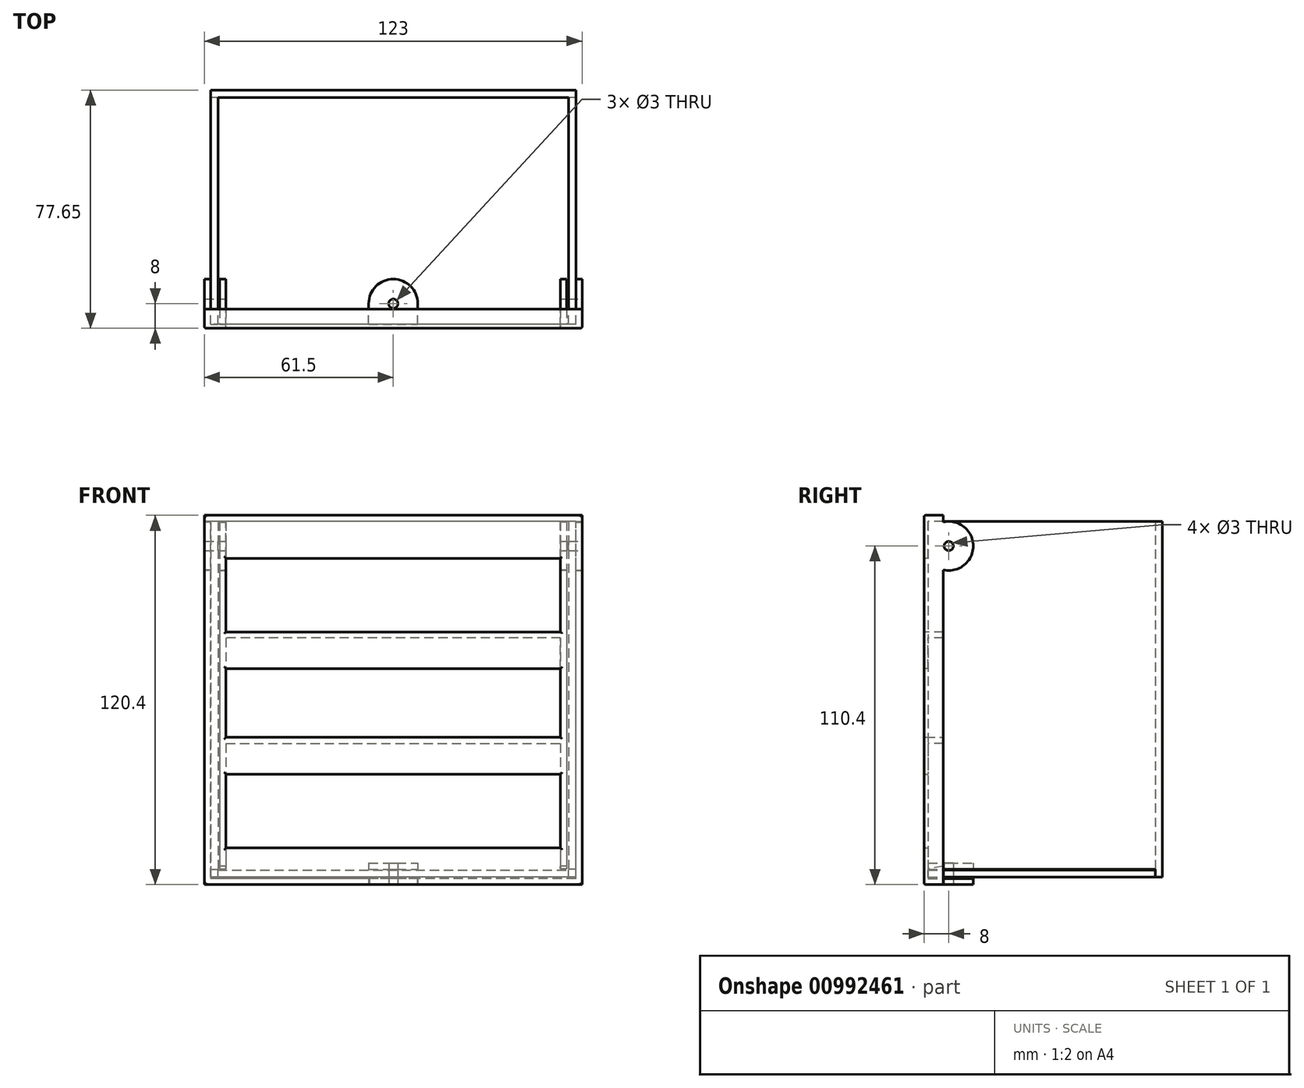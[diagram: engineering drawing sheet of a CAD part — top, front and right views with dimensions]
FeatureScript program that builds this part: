
annotation { "Feature Type Name" : "Feature", "Feature Type Description" : "" }
export const myFeature = defineFeature(function(context is Context, id is Id, definition is map)
    precondition{}
    {
        {
            var Q0;
            Q0=qCreatedBy(makeId("Front.planeOp"),FACE);
            var sketch = newSketch(context, id + "F0", { "sketchPlane" : qUnion([Q0])});
            skLineSegment(sketch, "E0.bottom", {"start": v(59.5, 0) * mm, "end": v(-59.5, 0) * mm});
            skLineSegment(sketch, "E0.top", {"start": v(59.5, 116) * mm, "end": v(-59.5, 116) * mm});
            skLineSegment(sketch, "E0.left", {"start": v(59.5, 0) * mm, "end": v(59.5, 116) * mm});
            skLineSegment(sketch, "E0.right", {"start": v(-59.5, 0) * mm, "end": v(-59.5, 116) * mm});
            skPoint(sketch, "E0.middle", {"position": v(0, 58) * mm});
            skSolve(sketch);
        }
        {
            var Q0;
            Q0=qSketchRegion(id+"F0",true);
            extrude(context, id + "F1", {"entities" : qUnion([Q0]), "oppositeDirection" : true, "depth" : 2.4 * mm, "offsetDistance" : 25 * mm});
        }
        {
            var Q0;
            Q0=makeQuery(id+"F1.opExtrude","CAP_FACE",FACE,{"disambiguationData":[OSD([sQuery(id+"F0.wireOp",EDGE,"E0.bottom"),sQuery(id+"F0.wireOp",EDGE,"E0.top"),sQuery(id+"F0.wireOp",EDGE,"E0.left"),sQuery(id+"F0.wireOp",EDGE,"E0.right")])],"isStart":true});
            var sketch = newSketch(context, id + "F2", { "sketchPlane" : qUnion([Q0])});
            skLineSegment(sketch, "E1.bottom", {"start": v(-59.5, 116) * mm, "end": v(-57.1, 116) * mm});
            skLineSegment(sketch, "E1.top", {"start": v(-59.5, 2.6) * mm, "end": v(-57.1, 2.6) * mm});
            skLineSegment(sketch, "E1.left", {"start": v(-59.5, 116) * mm, "end": v(-59.5, 2.6) * mm});
            skLineSegment(sketch, "E1.right", {"start": v(-57.1, 116) * mm, "end": v(-57.1, 2.6) * mm});
            skLineSegment(sketch, "E2.bottom", {"start": v(59.5, 116) * mm, "end": v(57.1, 116) * mm});
            skLineSegment(sketch, "E2.top", {"start": v(59.5, 2.6) * mm, "end": v(57.1, 2.6) * mm});
            skLineSegment(sketch, "E2.left", {"start": v(59.5, 116) * mm, "end": v(59.5, 2.6) * mm});
            skLineSegment(sketch, "E2.right", {"start": v(57.1, 116) * mm, "end": v(57.1, 2.6) * mm});
            skSolve(sketch);
        }
        {
            var Q0;
            Q0=qSketchRegion(id+"F2",true);
            extrude(context, id + "F3", {"entities" : qUnion([Q0]), "operationType" : NewBodyOperationType.ADD, "depth" : 74 * mm, "offsetDistance" : 25 * mm});
        }
        {
            var Q0;
            Q0=makeQuery(id+"F1.opExtrude","CAP_FACE",FACE,{"disambiguationData":[OSD([sQuery(id+"F0.wireOp",EDGE,"E0.bottom"),sQuery(id+"F0.wireOp",EDGE,"E0.top"),sQuery(id+"F0.wireOp",EDGE,"E0.left"),sQuery(id+"F0.wireOp",EDGE,"E0.right")])],"isStart":true});
            var sketch = newSketch(context, id + "F4", { "sketchPlane" : qUnion([Q0])});
            skLineSegment(sketch, "E3.bottom", {"start": v(-57.1, 0) * mm, "end": v(57.1, 0) * mm});
            skLineSegment(sketch, "E3.top", {"start": v(-57.1, 2.4) * mm, "end": v(57.1, 2.4) * mm});
            skLineSegment(sketch, "E3.left", {"start": v(-57.1, 0) * mm, "end": v(-57.1, 2.4) * mm});
            skLineSegment(sketch, "E3.right", {"start": v(57.1, 0) * mm, "end": v(57.1, 2.4) * mm});
            skSolve(sketch);
        }
        {
            var Q0;
            Q0=qSketchRegion(id+"F4",true);
            var Q1;
            Q1=makeQuery(id+"F3.opExtrude","CAP_FACE",FACE,{"disambiguationData":[OSD([sQuery(id+"F2.wireOp",EDGE,"E1.bottom"),sQuery(id+"F2.wireOp",EDGE,"E1.top"),sQuery(id+"F2.wireOp",EDGE,"E1.left"),sQuery(id+"F2.wireOp",EDGE,"E1.right")])],"isStart":false});
            extrude(context, id + "F5", {"entities" : qUnion([Q0]), "operationType" : NewBodyOperationType.ADD, "endBound" : BoundingType.UP_TO_SURFACE, "depth" : 36.25 * mm, "endBoundEntityFace" : qUnion([Q1]), "offsetDistance" : 25 * mm});
        }
        {
            var Q0;
            Q0=makeQuery(id+"F3.opExtrude","CAP_FACE",FACE,{"disambiguationData":[OSD([sQuery(id+"F2.wireOp",EDGE,"E1.bottom"),sQuery(id+"F2.wireOp",EDGE,"E1.top"),sQuery(id+"F2.wireOp",EDGE,"E1.left"),sQuery(id+"F2.wireOp",EDGE,"E1.right")])],"isStart":false});
            var sketch = newSketch(context, id + "F6", { "sketchPlane" : qUnion([Q0])});
            skLineSegment(sketch, "E4.bottom", {"start": v(59.5, 116) * mm, "end": v(-59.5, 116) * mm});
            skLineSegment(sketch, "E4.top", {"start": v(59.5, 104) * mm, "end": v(-59.5, 104) * mm});
            skLineSegment(sketch, "E4.left", {"start": v(59.5, 116) * mm, "end": v(59.5, 104) * mm});
            skPoint(sketch, "E4.middle", {"position": v(0, 110) * mm});
            skLineSegment(sketch, "E5.bottom", {"start": v(59.5, 80) * mm, "end": v(-59.5, 80) * mm});
            skLineSegment(sketch, "E5.top", {"start": v(59.5, 68) * mm, "end": v(-59.5, 68) * mm});
            skLineSegment(sketch, "E5.left", {"start": v(59.5, 80) * mm, "end": v(59.5, 68) * mm});
            skLineSegment(sketch, "E5.right", {"start": v(-59.5, 80) * mm, "end": v(-59.5, 68) * mm});
            skPoint(sketch, "E5.middle", {"position": v(0, 74) * mm});
            skLineSegment(sketch, "E6.bottom", {"start": v(59.5, 9.6) * mm, "end": v(-59.5, 9.6) * mm});
            skLineSegment(sketch, "E6.top", {"start": v(59.5, -2.4) * mm, "end": v(-59.5, -2.4) * mm});
            skLineSegment(sketch, "E6.left", {"start": v(59.5, 9.6) * mm, "end": v(59.5, -2.4) * mm});
            skLineSegment(sketch, "E6.right", {"start": v(-59.5, 9.6) * mm, "end": v(-59.5, -2.4) * mm});
            skPoint(sketch, "E6.middle", {"position": v(0, 3.6) * mm});
            skLineSegment(sketch, "E7.bottom", {"start": v(59.5, 45.6) * mm, "end": v(-59.5, 45.6) * mm});
            skLineSegment(sketch, "E7.top", {"start": v(59.5, 33.6) * mm, "end": v(-59.5, 33.6) * mm});
            skLineSegment(sketch, "E7.left", {"start": v(59.5, 45.6) * mm, "end": v(59.5, 33.6) * mm});
            skLineSegment(sketch, "E7.right", {"start": v(-59.5, 45.6) * mm, "end": v(-59.5, 33.6) * mm});
            skPoint(sketch, "E7.middle", {"position": v(0, 39.6) * mm});
            skLineSegment(sketch, "E8", {"start": v(-59.5, 116) * mm, "end": v(-59.5, 104) * mm});
            skSolve(sketch);
        }
        {
            var Q0;
            Q0=qSketchRegion(id+"F6",true);
            extrude(context, id + "F7", {"entities" : qUnion([Q0]), "depth" : 1.25 * mm, "offsetDistance" : 25 * mm});
        }
        {
            var Q0;
            Q0=makeQuery(id+"F3.opExtrude","CAP_FACE",FACE,{"disambiguationData":[OSD([sQuery(id+"F2.wireOp",EDGE,"E2.bottom"),sQuery(id+"F2.wireOp",EDGE,"E2.top"),sQuery(id+"F2.wireOp",EDGE,"E2.left"),sQuery(id+"F2.wireOp",EDGE,"E2.right")])],"isStart":false});
            var sketch = newSketch(context, id + "F8", { "sketchPlane" : qUnion([Q0])});
            skLineSegment(sketch, "E9.bottom", {"start": v(61.5, 116) * mm, "end": v(59.5, 116) * mm});
            skLineSegment(sketch, "E9.top", {"start": v(61.5, -2.4) * mm, "end": v(59.5, -2.4) * mm});
            skLineSegment(sketch, "E9.left", {"start": v(61.5, 116) * mm, "end": v(61.5, -2.4) * mm});
            skLineSegment(sketch, "E9.right", {"start": v(59.5, 116) * mm, "end": v(59.5, -2.4) * mm});
            skLineSegment(sketch, "E10.bottom", {"start": v(-59.5, 116) * mm, "end": v(-61.5, 116) * mm});
            skLineSegment(sketch, "E10.top", {"start": v(-59.5, -2.4) * mm, "end": v(-61.5, -2.4) * mm});
            skLineSegment(sketch, "E10.left", {"start": v(-59.5, 116) * mm, "end": v(-59.5, -2.4) * mm});
            skLineSegment(sketch, "E10.right", {"start": v(-61.5, 116) * mm, "end": v(-61.5, -2.4) * mm});
            skLineSegment(sketch, "E11.bottom", {"start": v(56.5, 116) * mm, "end": v(54.5, 116) * mm});
            skLineSegment(sketch, "E11.top", {"start": v(56.5, 2.6) * mm, "end": v(54.5, 2.6) * mm});
            skLineSegment(sketch, "E11.left", {"start": v(56.5, 116) * mm, "end": v(56.5, 2.6) * mm});
            skLineSegment(sketch, "E11.right", {"start": v(54.5, 116) * mm, "end": v(54.5, 2.6) * mm});
            skLineSegment(sketch, "E12.bottom", {"start": v(-56.5, 116) * mm, "end": v(-54.5, 116) * mm});
            skLineSegment(sketch, "E12.top", {"start": v(-56.5, 2.6) * mm, "end": v(-54.5, 2.6) * mm});
            skLineSegment(sketch, "E12.left", {"start": v(-56.5, 116) * mm, "end": v(-56.5, 2.6) * mm});
            skLineSegment(sketch, "E12.right", {"start": v(-54.5, 116) * mm, "end": v(-54.5, 2.6) * mm});
            skSolve(sketch);
        }
        {
            var Q0;
            Q0=qSketchRegion(id+"F8",true);
            var Q1;
            Q1=makeQuery(id+"F7.opExtrude","CAP_FACE",FACE,{"disambiguationData":[OSD([sQuery(id+"F6.wireOp",EDGE,"E6.bottom"),sQuery(id+"F6.wireOp",EDGE,"E6.top"),sQuery(id+"F6.wireOp",EDGE,"E6.left"),sQuery(id+"F6.wireOp",EDGE,"E6.right")])],"isStart":false});
            extrude(context, id + "F9", {"entities" : qUnion([Q0]), "oppositeDirection" : true, "depth" : 5 * mm, "offsetDistance" : 25 * mm, "hasSecondDirection" : true, "secondDirectionBound" : SecondDirectionBoundingType.UP_TO_SURFACE, "secondDirectionOppositeDirection" : false, "secondDirectionDepth" : 2.4 * mm, "secondDirectionBoundEntityFace" : qUnion([Q1])});
        }
        {
            var Q0;
            Q0=makeQuery(id+"F7.opExtrude","SWEPT_BODY",BODY,{"disambiguationData":[OSD([sQuery(id+"F6.wireOp",EDGE,"E6.bottom"),sQuery(id+"F6.wireOp",EDGE,"E6.top"),sQuery(id+"F6.wireOp",EDGE,"E6.left"),sQuery(id+"F6.wireOp",EDGE,"E6.right")])]});
            var Q1;
            Q1=makeQuery(id+"F7.opExtrude","SWEPT_BODY",BODY,{"disambiguationData":[OSD([sQuery(id+"F6.wireOp",EDGE,"E7.bottom"),sQuery(id+"F6.wireOp",EDGE,"E7.top"),sQuery(id+"F6.wireOp",EDGE,"E7.left"),sQuery(id+"F6.wireOp",EDGE,"E7.right")])]});
            var Q2;
            Q2=makeQuery(id+"F9.opExtrude","SWEPT_BODY",BODY,{"disambiguationData":[OSD([sQuery(id+"F8.wireOp",EDGE,"E11.bottom"),sQuery(id+"F8.wireOp",EDGE,"E11.top"),sQuery(id+"F8.wireOp",EDGE,"E11.left"),sQuery(id+"F8.wireOp",EDGE,"E11.right")])]});
            var Q3;
            Q3=makeQuery(id+"F7.opExtrude","SWEPT_BODY",BODY,{"disambiguationData":[OSD([sQuery(id+"F6.wireOp",EDGE,"E4.bottom"),sQuery(id+"F6.wireOp",EDGE,"E4.top"),sQuery(id+"F6.wireOp",EDGE,"E4.left"),sQuery(id+"F6.wireOp",EDGE,"E8")])]});
            var Q4;
            Q4=makeQuery(id+"F9.opExtrude","SWEPT_BODY",BODY,{"disambiguationData":[OSD([sQuery(id+"F8.wireOp",EDGE,"E9.bottom"),sQuery(id+"F8.wireOp",EDGE,"E9.top"),sQuery(id+"F8.wireOp",EDGE,"E9.left"),sQuery(id+"F8.wireOp",EDGE,"E9.right")])]});
            var Q5;
            Q5=makeQuery(id+"F7.opExtrude","SWEPT_BODY",BODY,{"disambiguationData":[OSD([sQuery(id+"F6.wireOp",EDGE,"E5.bottom"),sQuery(id+"F6.wireOp",EDGE,"E5.top"),sQuery(id+"F6.wireOp",EDGE,"E5.left"),sQuery(id+"F6.wireOp",EDGE,"E5.right")])]});
            var Q6;
            Q6=makeQuery(id+"F9.opExtrude","SWEPT_BODY",BODY,{"disambiguationData":[OSD([sQuery(id+"F8.wireOp",EDGE,"E10.bottom"),sQuery(id+"F8.wireOp",EDGE,"E10.top"),sQuery(id+"F8.wireOp",EDGE,"E10.left"),sQuery(id+"F8.wireOp",EDGE,"E10.right")])]});
            var Q7;
            Q7=makeQuery(id+"F9.opExtrude","SWEPT_BODY",BODY,{"disambiguationData":[OSD([sQuery(id+"F8.wireOp",EDGE,"E12.bottom"),sQuery(id+"F8.wireOp",EDGE,"E12.top"),sQuery(id+"F8.wireOp",EDGE,"E12.left"),sQuery(id+"F8.wireOp",EDGE,"E12.right")])]});
            booleanBodies(context, id + "F10", {"operationType" : BooleanOperationType.UNION, "tools" : qUnion([Q0, Q1, Q2, Q3, Q4, Q5, Q6, Q7])});
        }
        {
            var Q0;
            Q0=makeQuery(id+"F9.opExtrude","SWEPT_FACE",FACE,{"disambiguationData":[OSD([sQuery(id+"F8.wireOp",EDGE,"E12.top")])]});
            var sketch = newSketch(context, id + "F11", { "sketchPlane" : qUnion([Q0])});
            skArc(sketch, "E13", {"start": v(-8, 67.25) * mm, "mid": v(0, 59.25) * mm, "end": v(8, 67.25) * mm});
            skLineSegment(sketch, "E14.bottom", {"start": v(-8, 75.25) * mm, "end": v(8, 75.25) * mm});
            skLineSegment(sketch, "E14.left", {"start": v(-8, 75.25) * mm, "end": v(-8, 67.25) * mm});
            skLineSegment(sketch, "E14.right", {"start": v(8, 75.25) * mm, "end": v(8, 67.25) * mm});
            skPoint(sketch, "E15.orphan", {"position": v(8, 59.25) * mm});
            skPoint(sketch, "E16.orphan", {"position": v(-8, 59.25) * mm});
            skSolve(sketch);
        }
        {
            var Q0;
            Q0 = qSketchRegion(id + "F11", true);
            extrude(context, id + "F12", {"entities" : qUnion([Q0]), "operationType" : NewBodyOperationType.ADD, "oppositeDirection" : true, "depth" : 2 * mm, "offsetDistance" : 25 * mm});
        }
        {
            var Q0;
            Q0=qCreatedBy(makeId("Right.planeOp"),FACE);
            var sketch = newSketch(context, id + "F13", { "sketchPlane" : qUnion([Q0])});
            skLineSegment(sketch, "E17.bottom", {"start": v(-74, -0.4) * mm, "end": v(-69, -0.4) * mm});
            skLineSegment(sketch, "E17.top", {"start": v(-74, -2.4) * mm, "end": v(-69, -2.4) * mm});
            skLineSegment(sketch, "E17.left", {"start": v(-74, -0.4) * mm, "end": v(-74, -2.4) * mm});
            skLineSegment(sketch, "E17.right", {"start": v(-69, -0.4) * mm, "end": v(-69, -2.4) * mm});
            skSolve(sketch);
        }
        {
            var Q0;
            Q0=qSketchRegion(id+"F13",true);
            var Q1;
            Q1=makeQuery(id+"F9.opExtrude","SWEPT_FACE",FACE,{"disambiguationData":[OSD([sQuery(id+"F8.wireOp",EDGE,"E9.right")])]});
            var Q2;
            Q2=makeQuery(id+"F9.opExtrude","SWEPT_FACE",FACE,{"disambiguationData":[OSD([sQuery(id+"F8.wireOp",EDGE,"E10.left")])]});
            extrude(context, id + "F14", {"entities" : qUnion([Q0]), "operationType" : NewBodyOperationType.ADD, "endBound" : BoundingType.UP_TO_SURFACE, "depth" : 25 * mm, "endBoundEntityFace" : qUnion([Q1]), "offsetDistance" : 25 * mm, "hasSecondDirection" : true, "secondDirectionBound" : SecondDirectionBoundingType.UP_TO_SURFACE, "secondDirectionOppositeDirection" : true, "secondDirectionDepth" : 25 * mm, "secondDirectionBoundEntityFace" : qUnion([Q2])});
        }
        {
            var Q0;
            Q0=makeQuery(id+"F10.opBoolean","MERGE",FACE,{"derivedFrom":[makeQuery(id+"F7.opExtrude","CAP_FACE",FACE,{"disambiguationData":[OSD([sQuery(id+"F6.wireOp",EDGE,"E4.bottom"),sQuery(id+"F6.wireOp",EDGE,"E4.top"),sQuery(id+"F6.wireOp",EDGE,"E4.left"),sQuery(id+"F6.wireOp",EDGE,"E8")])],"isStart":false}),makeQuery(id+"F7.opExtrude","CAP_FACE",FACE,{"disambiguationData":[OSD([sQuery(id+"F6.wireOp",EDGE,"E5.bottom"),sQuery(id+"F6.wireOp",EDGE,"E5.top"),sQuery(id+"F6.wireOp",EDGE,"E5.left"),sQuery(id+"F6.wireOp",EDGE,"E5.right")])],"isStart":false}),makeQuery(id+"F7.opExtrude","CAP_FACE",FACE,{"disambiguationData":[OSD([sQuery(id+"F6.wireOp",EDGE,"E6.bottom"),sQuery(id+"F6.wireOp",EDGE,"E6.top"),sQuery(id+"F6.wireOp",EDGE,"E6.left"),sQuery(id+"F6.wireOp",EDGE,"E6.right")])],"isStart":false}),makeQuery(id+"F7.opExtrude","CAP_FACE",FACE,{"disambiguationData":[OSD([sQuery(id+"F6.wireOp",EDGE,"E7.bottom"),sQuery(id+"F6.wireOp",EDGE,"E7.top"),sQuery(id+"F6.wireOp",EDGE,"E7.left"),sQuery(id+"F6.wireOp",EDGE,"E7.right")])],"isStart":false}),makeQuery(id+"F9.opExtrude","CAP_FACE",FACE,{"disambiguationData":[OSD([sQuery(id+"F8.wireOp",EDGE,"E9.bottom"),sQuery(id+"F8.wireOp",EDGE,"E9.top"),sQuery(id+"F8.wireOp",EDGE,"E9.left"),sQuery(id+"F8.wireOp",EDGE,"E9.right")])],"isStart":true}),makeQuery(id+"F9.opExtrude","CAP_FACE",FACE,{"disambiguationData":[OSD([sQuery(id+"F8.wireOp",EDGE,"E10.bottom"),sQuery(id+"F8.wireOp",EDGE,"E10.top"),sQuery(id+"F8.wireOp",EDGE,"E10.left"),sQuery(id+"F8.wireOp",EDGE,"E10.right")])],"isStart":true}),makeQuery(id+"F9.opExtrude","CAP_FACE",FACE,{"disambiguationData":[OSD([sQuery(id+"F8.wireOp",EDGE,"E11.bottom"),sQuery(id+"F8.wireOp",EDGE,"E11.top"),sQuery(id+"F8.wireOp",EDGE,"E11.left"),sQuery(id+"F8.wireOp",EDGE,"E11.right")])],"isStart":true}),makeQuery(id+"F9.opExtrude","CAP_FACE",FACE,{"disambiguationData":[OSD([sQuery(id+"F8.wireOp",EDGE,"E12.bottom"),sQuery(id+"F8.wireOp",EDGE,"E12.top"),sQuery(id+"F8.wireOp",EDGE,"E12.left"),sQuery(id+"F8.wireOp",EDGE,"E12.right")])],"isStart":true})]});
            var sketch = newSketch(context, id + "F15", { "sketchPlane" : qUnion([Q0])});
            skLineSegment(sketch, "E18.bottom", {"start": v(-61.5, 116) * mm, "end": v(-56.5, 116) * mm});
            skLineSegment(sketch, "E18.top", {"start": v(-61.5, -2.4) * mm, "end": v(-56.5, -2.4) * mm});
            skLineSegment(sketch, "E18.left", {"start": v(-61.5, 116) * mm, "end": v(-61.5, -2.4) * mm});
            skLineSegment(sketch, "E18.right", {"start": v(-56.5, 116) * mm, "end": v(-56.5, -2.4) * mm});
            skLineSegment(sketch, "E19.bottom", {"start": v(61.5, 116) * mm, "end": v(56.5, 116) * mm});
            skLineSegment(sketch, "E19.top", {"start": v(61.5, -2.4) * mm, "end": v(56.5, -2.4) * mm});
            skLineSegment(sketch, "E19.left", {"start": v(61.5, 116) * mm, "end": v(61.5, -2.4) * mm});
            skLineSegment(sketch, "E19.right", {"start": v(56.5, 116) * mm, "end": v(56.5, -2.4) * mm});
            skSolve(sketch);
        }
        {
            var Q0;
            Q0=qSketchRegion(id+"F15",true);
            var Q1;
            {var subQ0=sQuery(id+"F6.wireOp",EDGE,"E4.top");var subQ1=sQuery(id+"F6.wireOp",EDGE,"E4.bottom");Q1=makeQuery(id+"F10.opBoolean","SPLIT",FACE,{"disambiguationData":[TD([makeQuery(id+"F9.opExtrude","SWEPT_FACE",FACE,{"disambiguationData":[OSD([sQuery(id+"F8.wireOp",EDGE,"E11.right")])]})])],"derivedFrom":makeQuery(id+"F7.opExtrude","CAP_FACE",FACE,{"disambiguationData":[OSD([subQ1,subQ0,sQuery(id+"F6.wireOp",EDGE,"E4.left"),sQuery(id+"F6.wireOp",EDGE,"E8")])],"isStart":true})});}
            extrude(context, id + "F16", {"entities" : qUnion([Q0]), "operationType" : NewBodyOperationType.ADD, "endBound" : BoundingType.UP_TO_SURFACE, "oppositeDirection" : true, "depth" : 25 * mm, "endBoundEntityFace" : qUnion([Q1]), "offsetDistance" : 25 * mm});
        }
        {
            var Q0;
            Q0=makeQuery(id+"F14.boolean.opBoolean","MERGE",FACE,{"derivedFrom":[makeQuery(id+"F10.opBoolean","MERGE",FACE,{"derivedFrom":[makeQuery(id+"F7.opExtrude","SWEPT_FACE",FACE,{"disambiguationData":[OSD([sQuery(id+"F6.wireOp",EDGE,"E6.top")])]}),makeQuery(id+"F9.opExtrude","SWEPT_FACE",FACE,{"disambiguationData":[OSD([sQuery(id+"F8.wireOp",EDGE,"E9.top")])]}),makeQuery(id+"F9.opExtrude","SWEPT_FACE",FACE,{"disambiguationData":[OSD([sQuery(id+"F8.wireOp",EDGE,"E10.top")])]})]}),makeQuery(id+"F14.opExtrude","SWEPT_FACE",FACE,{"disambiguationData":[OSD([sQuery(id+"F13.wireOp",EDGE,"E17.top")])]})]});
            var sketch = newSketch(context, id + "F17", { "sketchPlane" : qUnion([Q0])});
            skCircle(sketch, "E20", {"center": v(0, 67.25) * mm, "radius": 8 * mm});
            skSolve(sketch);
        }
        {
            var Q0;
            Q0=qSketchRegion(id+"F17",true);
            var Q1;
            Q1=makeQuery(id+"F14.opExtrude","SWEPT_FACE",FACE,{"disambiguationData":[OSD([sQuery(id+"F13.wireOp",EDGE,"E17.bottom")])]});
            extrude(context, id + "F18", {"entities" : qUnion([Q0]), "operationType" : NewBodyOperationType.ADD, "endBound" : BoundingType.UP_TO_SURFACE, "oppositeDirection" : true, "depth" : 25 * mm, "endBoundEntityFace" : qUnion([Q1]), "offsetDistance" : 25 * mm});
        }
        {
            var Q0;
            Q0=makeQuery(id+"F18.boolean.opBoolean","MERGE",FACE,{"derivedFrom":[makeQuery(id+"F14.boolean.opBoolean","MERGE",FACE,{"derivedFrom":[makeQuery(id+"F10.opBoolean","MERGE",FACE,{"derivedFrom":[makeQuery(id+"F7.opExtrude","SWEPT_FACE",FACE,{"disambiguationData":[OSD([sQuery(id+"F6.wireOp",EDGE,"E6.top")])]}),makeQuery(id+"F9.opExtrude","SWEPT_FACE",FACE,{"disambiguationData":[OSD([sQuery(id+"F8.wireOp",EDGE,"E9.top")])]}),makeQuery(id+"F9.opExtrude","SWEPT_FACE",FACE,{"disambiguationData":[OSD([sQuery(id+"F8.wireOp",EDGE,"E10.top")])]})]}),makeQuery(id+"F14.opExtrude","SWEPT_FACE",FACE,{"disambiguationData":[OSD([sQuery(id+"F13.wireOp",EDGE,"E17.top")])]})]}),makeQuery(id+"F18.opExtrude","CAP_FACE",FACE,{"disambiguationData":[OSD([sQuery(id+"F17.wireOp",EDGE,"E20")])],"isStart":true})]});
            var sketch = newSketch(context, id + "F19", { "sketchPlane" : qUnion([Q0])});
            skCircle(sketch, "E21", {"center": v(0, 67.25) * mm, "radius": 1.5 * mm});
            skSolve(sketch);
        }
        {
            var Q0;
            Q0=qSketchRegion(id+"F19",true);
            var Q1;
            Q1=makeQuery(id+"F12.opExtrude","CAP_FACE",FACE,{"disambiguationData":[OSD([sQuery(id+"F11.wireOp",EDGE,"E13"),sQuery(id+"F11.wireOp",EDGE,"E14.bottom"),sQuery(id+"F11.wireOp",EDGE,"E14.left"),sQuery(id+"F11.wireOp",EDGE,"E14.right")])],"isStart":false});
            extrude(context, id + "F20", {"entities" : qUnion([Q0]), "operationType" : NewBodyOperationType.REMOVE, "endBound" : BoundingType.UP_TO_SURFACE, "oppositeDirection" : true, "depth" : 25 * mm, "endBoundEntityFace" : qUnion([Q1]), "offsetDistance" : 25 * mm});
        }
        {
            var Q0;
            Q0=makeQuery(id+"F9.opExtrude","SWEPT_FACE",FACE,{"disambiguationData":[OSD([sQuery(id+"F8.wireOp",EDGE,"E10.right")])]});
            var sketch = newSketch(context, id + "F21", { "sketchPlane" : qUnion([Q0])});
            skCircle(sketch, "E22", {"center": v(67.25, 108) * mm, "radius": 8 * mm});
            skSolve(sketch);
        }
        {
            var Q0;
            Q0=qSketchRegion(id+"F21",true);
            var Q1;
            Q1=makeQuery(id+"F9.opExtrude","SWEPT_FACE",FACE,{"disambiguationData":[OSD([sQuery(id+"F8.wireOp",EDGE,"E10.left")])]});
            extrude(context, id + "F22", {"entities" : qUnion([Q0]), "operationType" : NewBodyOperationType.ADD, "endBound" : BoundingType.UP_TO_SURFACE, "oppositeDirection" : true, "depth" : 25 * mm, "endBoundEntityFace" : qUnion([Q1]), "offsetDistance" : 25 * mm});
        }
        {
            var Q0;
            Q0=makeQuery(id+"F9.opExtrude","SWEPT_FACE",FACE,{"disambiguationData":[OSD([sQuery(id+"F8.wireOp",EDGE,"E12.right")])]});
            var sketch = newSketch(context, id + "F23", { "sketchPlane" : qUnion([Q0])});
            skCircle(sketch, "E23", {"center": v(-67.25, 108) * mm, "radius": 8 * mm});
            skSolve(sketch);
        }
        {
            var Q0;
            Q0=qSketchRegion(id+"F23",true);
            var Q1;
            Q1=makeQuery(id+"F9.opExtrude","SWEPT_FACE",FACE,{"disambiguationData":[OSD([sQuery(id+"F8.wireOp",EDGE,"E12.left")])]});
            extrude(context, id + "F24", {"entities" : qUnion([Q0]), "operationType" : NewBodyOperationType.ADD, "endBound" : BoundingType.UP_TO_SURFACE, "oppositeDirection" : true, "depth" : 25 * mm, "endBoundEntityFace" : qUnion([Q1]), "offsetDistance" : 25 * mm});
        }
        {
            var Q0;
            Q0=makeQuery(id+"F9.opExtrude","SWEPT_FACE",FACE,{"disambiguationData":[OSD([sQuery(id+"F8.wireOp",EDGE,"E9.left")])]});
            var sketch = newSketch(context, id + "F25", { "sketchPlane" : qUnion([Q0])});
            skCircle(sketch, "E24", {"center": v(-67.25, 108) * mm, "radius": 8 * mm});
            skSolve(sketch);
        }
        {
            var Q0;
            Q0=qSketchRegion(id+"F25",true);
            var Q1;
            Q1=makeQuery(id+"F9.opExtrude","SWEPT_FACE",FACE,{"disambiguationData":[OSD([sQuery(id+"F8.wireOp",EDGE,"E9.right")])]});
            extrude(context, id + "F26", {"entities" : qUnion([Q0]), "operationType" : NewBodyOperationType.ADD, "endBound" : BoundingType.UP_TO_SURFACE, "oppositeDirection" : true, "depth" : 25 * mm, "endBoundEntityFace" : qUnion([Q1]), "offsetDistance" : 25 * mm});
        }
        {
            var Q0;
            Q0=makeQuery(id+"F9.opExtrude","SWEPT_FACE",FACE,{"disambiguationData":[OSD([sQuery(id+"F8.wireOp",EDGE,"E11.right")])]});
            var sketch = newSketch(context, id + "F27", { "sketchPlane" : qUnion([Q0])});
            skCircle(sketch, "E25", {"center": v(67.25, 108) * mm, "radius": 8 * mm});
            skSolve(sketch);
        }
        {
            var Q0;
            Q0=qSketchRegion(id+"F27",true);
            var Q1;
            Q1=makeQuery(id+"F9.opExtrude","SWEPT_FACE",FACE,{"disambiguationData":[OSD([sQuery(id+"F8.wireOp",EDGE,"E11.left")])]});
            extrude(context, id + "F28", {"entities" : qUnion([Q0]), "operationType" : NewBodyOperationType.ADD, "endBound" : BoundingType.UP_TO_SURFACE, "oppositeDirection" : true, "depth" : 25 * mm, "endBoundEntityFace" : qUnion([Q1]), "offsetDistance" : 25 * mm});
        }
        {
            var Q0;
            Q0=makeQuery(id+"F26.boolean.opBoolean","MERGE",FACE,{"derivedFrom":[makeQuery(id+"F9.opExtrude","SWEPT_FACE",FACE,{"disambiguationData":[OSD([sQuery(id+"F8.wireOp",EDGE,"E9.left")])]}),makeQuery(id+"F26.opExtrude","CAP_FACE",FACE,{"disambiguationData":[OSD([sQuery(id+"F25.wireOp",EDGE,"E24")])],"isStart":true})]});
            var sketch = newSketch(context, id + "F29", { "sketchPlane" : qUnion([Q0])});
            skCircle(sketch, "E26", {"center": v(-67.25, 108) * mm, "radius": 1.5 * mm});
            skSolve(sketch);
        }
        {
            var Q0;
            Q0=qSketchRegion(id+"F29",true);
            var Q1;
            Q1=makeQuery(id+"F22.boolean.opBoolean","MERGE",FACE,{"derivedFrom":[makeQuery(id+"F9.opExtrude","SWEPT_FACE",FACE,{"disambiguationData":[OSD([sQuery(id+"F8.wireOp",EDGE,"E10.right")])]}),makeQuery(id+"F22.opExtrude","CAP_FACE",FACE,{"disambiguationData":[OSD([sQuery(id+"F21.wireOp",EDGE,"E22")])],"isStart":true})]});
            extrude(context, id + "F30", {"entities" : qUnion([Q0]), "operationType" : NewBodyOperationType.REMOVE, "endBound" : BoundingType.UP_TO_SURFACE, "oppositeDirection" : true, "depth" : 25 * mm, "endBoundEntityFace" : qUnion([Q1]), "offsetDistance" : 25 * mm});
        }
        {
            var Q0;
            Q0=makeQuery(id+"F9.opExtrude","CAP_EDGE",EDGE,{"disambiguationData":[OSD([sQuery(id+"F8.wireOp",EDGE,"E11.top")])],"isStart":false});
            chamfer(context, id + "F31", {"entities" : qUnion([Q0]), "chamferType" : ChamferType.TWO_OFFSETS, "width1" : 1 * mm, "oppositeDirection" : false, "width2" : 6 * mm, "tangentPropagation" : true});
        }
        {
            var Q0;
            Q0=makeQuery(id+"F9.opExtrude","CAP_EDGE",EDGE,{"disambiguationData":[OSD([sQuery(id+"F8.wireOp",EDGE,"E12.top")])],"isStart":false});
            chamfer(context, id + "F32", {"entities" : qUnion([Q0]), "chamferType" : ChamferType.TWO_OFFSETS, "width1" : 6 * mm, "oppositeDirection" : false, "width2" : 1 * mm, "tangentPropagation" : true});
        }
        {
            var Q0;
            Q0=makeQuery(id+"F16.boolean.opBoolean","MERGE",FACE,{"derivedFrom":[makeQuery(id+"F10.opBoolean","MERGE",FACE,{"derivedFrom":[makeQuery(id+"F7.opExtrude","CAP_FACE",FACE,{"disambiguationData":[OSD([sQuery(id+"F6.wireOp",EDGE,"E4.bottom"),sQuery(id+"F6.wireOp",EDGE,"E4.top"),sQuery(id+"F6.wireOp",EDGE,"E4.left"),sQuery(id+"F6.wireOp",EDGE,"E8")])],"isStart":false}),makeQuery(id+"F7.opExtrude","CAP_FACE",FACE,{"disambiguationData":[OSD([sQuery(id+"F6.wireOp",EDGE,"E5.bottom"),sQuery(id+"F6.wireOp",EDGE,"E5.top"),sQuery(id+"F6.wireOp",EDGE,"E5.left"),sQuery(id+"F6.wireOp",EDGE,"E5.right")])],"isStart":false}),makeQuery(id+"F7.opExtrude","CAP_FACE",FACE,{"disambiguationData":[OSD([sQuery(id+"F6.wireOp",EDGE,"E6.bottom"),sQuery(id+"F6.wireOp",EDGE,"E6.top"),sQuery(id+"F6.wireOp",EDGE,"E6.left"),sQuery(id+"F6.wireOp",EDGE,"E6.right")])],"isStart":false}),makeQuery(id+"F7.opExtrude","CAP_FACE",FACE,{"disambiguationData":[OSD([sQuery(id+"F6.wireOp",EDGE,"E7.bottom"),sQuery(id+"F6.wireOp",EDGE,"E7.top"),sQuery(id+"F6.wireOp",EDGE,"E7.left"),sQuery(id+"F6.wireOp",EDGE,"E7.right")])],"isStart":false}),makeQuery(id+"F9.opExtrude","CAP_FACE",FACE,{"disambiguationData":[OSD([sQuery(id+"F8.wireOp",EDGE,"E9.bottom"),sQuery(id+"F8.wireOp",EDGE,"E9.top"),sQuery(id+"F8.wireOp",EDGE,"E9.left"),sQuery(id+"F8.wireOp",EDGE,"E9.right")])],"isStart":true}),makeQuery(id+"F9.opExtrude","CAP_FACE",FACE,{"disambiguationData":[OSD([sQuery(id+"F8.wireOp",EDGE,"E10.bottom"),sQuery(id+"F8.wireOp",EDGE,"E10.top"),sQuery(id+"F8.wireOp",EDGE,"E10.left"),sQuery(id+"F8.wireOp",EDGE,"E10.right")])],"isStart":true}),makeQuery(id+"F9.opExtrude","CAP_FACE",FACE,{"disambiguationData":[OSD([sQuery(id+"F8.wireOp",EDGE,"E11.bottom"),sQuery(id+"F8.wireOp",EDGE,"E11.top"),sQuery(id+"F8.wireOp",EDGE,"E11.left"),sQuery(id+"F8.wireOp",EDGE,"E11.right")])],"isStart":true}),makeQuery(id+"F9.opExtrude","CAP_FACE",FACE,{"disambiguationData":[OSD([sQuery(id+"F8.wireOp",EDGE,"E12.bottom"),sQuery(id+"F8.wireOp",EDGE,"E12.top"),sQuery(id+"F8.wireOp",EDGE,"E12.left"),sQuery(id+"F8.wireOp",EDGE,"E12.right")])],"isStart":true})]}),makeQuery(id+"F16.opExtrude","CAP_FACE",FACE,{"disambiguationData":[OSD([sQuery(id+"F15.wireOp",EDGE,"E18.bottom"),sQuery(id+"F15.wireOp",EDGE,"E18.top"),sQuery(id+"F15.wireOp",EDGE,"E18.left"),sQuery(id+"F15.wireOp",EDGE,"E18.right")])],"isStart":true}),makeQuery(id+"F16.opExtrude","CAP_FACE",FACE,{"disambiguationData":[OSD([sQuery(id+"F15.wireOp",EDGE,"E19.bottom"),sQuery(id+"F15.wireOp",EDGE,"E19.top"),sQuery(id+"F15.wireOp",EDGE,"E19.left"),sQuery(id+"F15.wireOp",EDGE,"E19.right")])],"isStart":true})]});
            var sketch = newSketch(context, id + "F33", { "sketchPlane" : qUnion([Q0])});
            skLineSegment(sketch, "E27.bottom", {"start": v(61.5, 116) * mm, "end": v(-61.5, 116) * mm});
            skLineSegment(sketch, "E27.top", {"start": v(61.5, 118) * mm, "end": v(-61.5, 118) * mm});
            skLineSegment(sketch, "E27.left", {"start": v(61.5, 116) * mm, "end": v(61.5, 118) * mm});
            skLineSegment(sketch, "E27.right", {"start": v(-61.5, 116) * mm, "end": v(-61.5, 118) * mm});
            skPoint(sketch, "E27.middle", {"position": v(0, 117) * mm});
            skLineSegment(sketch, "E28.bottom", {"start": v(54.5, 80) * mm, "end": v(-54.5, 80) * mm});
            skLineSegment(sketch, "E28.top", {"start": v(54.5, 78) * mm, "end": v(-54.5, 78) * mm});
            skLineSegment(sketch, "E28.left", {"start": v(54.5, 80) * mm, "end": v(54.5, 78) * mm});
            skLineSegment(sketch, "E28.right", {"start": v(-54.5, 80) * mm, "end": v(-54.5, 78) * mm});
            skPoint(sketch, "E28.middle", {"position": v(0, 79) * mm});
            skLineSegment(sketch, "E29.bottom", {"start": v(-54.5, 43.6) * mm, "end": v(54.5, 43.6) * mm});
            skLineSegment(sketch, "E29.top", {"start": v(-54.5, 45.6) * mm, "end": v(54.5, 45.6) * mm});
            skLineSegment(sketch, "E29.left", {"start": v(-54.5, 43.6) * mm, "end": v(-54.5, 45.6) * mm});
            skLineSegment(sketch, "E29.right", {"start": v(54.5, 43.6) * mm, "end": v(54.5, 45.6) * mm});
            skPoint(sketch, "E29.middle", {"position": v(0, 44.6) * mm});
            skSolve(sketch);
        }
        {
            var Q0;
            Q0=qSketchRegion(id+"F33",true);
            var Q1;
            {var subQ1=sQuery(id+"F8.wireOp",EDGE,"E10.top");var subQ2=sQuery(id+"F8.wireOp",EDGE,"E10.bottom");var subQ3=sQuery(id+"F8.wireOp",EDGE,"E10.left");var subQ4=sQuery(id+"F8.wireOp",EDGE,"E10.right");var subQ5=sQuery(id+"F8.wireOp",EDGE,"E9.bottom");var subQ6=sQuery(id+"F8.wireOp",EDGE,"E9.top");Q1=makeQuery(id+"F18.boolean.opBoolean","SPLIT",FACE,{"disambiguationData":[TD([makeQuery(id+"F9.opExtrude","SWEPT_FACE",FACE,{"disambiguationData":[OSD([subQ3])]})])],"derivedFrom":makeQuery(id+"F14.boolean.opBoolean","MERGE",FACE,{"derivedFrom":[makeQuery(id+"F9.opExtrude","CAP_FACE",FACE,{"disambiguationData":[OSD([subQ5,subQ6,sQuery(id+"F8.wireOp",EDGE,"E9.left"),sQuery(id+"F8.wireOp",EDGE,"E9.right")])],"isStart":false}),makeQuery(id+"F9.opExtrude","CAP_FACE",FACE,{"disambiguationData":[OSD([subQ2,subQ1,subQ3,subQ4])],"isStart":false}),makeQuery(id+"F14.opExtrude","SWEPT_FACE",FACE,{"disambiguationData":[OSD([sQuery(id+"F13.wireOp",EDGE,"E17.right")])]})]})});}
            extrude(context, id + "F34", {"entities" : qUnion([Q0]), "operationType" : NewBodyOperationType.ADD, "endBound" : BoundingType.UP_TO_SURFACE, "oppositeDirection" : true, "depth" : 25 * mm, "endBoundEntityFace" : qUnion([Q1]), "offsetDistance" : 25 * mm});
        }
        {
            var Q0;
            Q0=makeQuery(id+"F34.boolean.opBoolean","MERGE",FACE,{"derivedFrom":[makeQuery(id+"F16.boolean.opBoolean","MERGE",FACE,{"derivedFrom":[makeQuery(id+"F10.opBoolean","MERGE",FACE,{"derivedFrom":[makeQuery(id+"F7.opExtrude","CAP_FACE",FACE,{"disambiguationData":[OSD([sQuery(id+"F6.wireOp",EDGE,"E4.bottom"),sQuery(id+"F6.wireOp",EDGE,"E4.top"),sQuery(id+"F6.wireOp",EDGE,"E4.left"),sQuery(id+"F6.wireOp",EDGE,"E8")])],"isStart":false}),makeQuery(id+"F7.opExtrude","CAP_FACE",FACE,{"disambiguationData":[OSD([sQuery(id+"F6.wireOp",EDGE,"E5.bottom"),sQuery(id+"F6.wireOp",EDGE,"E5.top"),sQuery(id+"F6.wireOp",EDGE,"E5.left"),sQuery(id+"F6.wireOp",EDGE,"E5.right")])],"isStart":false}),makeQuery(id+"F7.opExtrude","CAP_FACE",FACE,{"disambiguationData":[OSD([sQuery(id+"F6.wireOp",EDGE,"E6.bottom"),sQuery(id+"F6.wireOp",EDGE,"E6.top"),sQuery(id+"F6.wireOp",EDGE,"E6.left"),sQuery(id+"F6.wireOp",EDGE,"E6.right")])],"isStart":false}),makeQuery(id+"F7.opExtrude","CAP_FACE",FACE,{"disambiguationData":[OSD([sQuery(id+"F6.wireOp",EDGE,"E7.bottom"),sQuery(id+"F6.wireOp",EDGE,"E7.top"),sQuery(id+"F6.wireOp",EDGE,"E7.left"),sQuery(id+"F6.wireOp",EDGE,"E7.right")])],"isStart":false}),makeQuery(id+"F9.opExtrude","CAP_FACE",FACE,{"disambiguationData":[OSD([sQuery(id+"F8.wireOp",EDGE,"E9.bottom"),sQuery(id+"F8.wireOp",EDGE,"E9.top"),sQuery(id+"F8.wireOp",EDGE,"E9.left"),sQuery(id+"F8.wireOp",EDGE,"E9.right")])],"isStart":true}),makeQuery(id+"F9.opExtrude","CAP_FACE",FACE,{"disambiguationData":[OSD([sQuery(id+"F8.wireOp",EDGE,"E10.bottom"),sQuery(id+"F8.wireOp",EDGE,"E10.top"),sQuery(id+"F8.wireOp",EDGE,"E10.left"),sQuery(id+"F8.wireOp",EDGE,"E10.right")])],"isStart":true}),makeQuery(id+"F9.opExtrude","CAP_FACE",FACE,{"disambiguationData":[OSD([sQuery(id+"F8.wireOp",EDGE,"E11.bottom"),sQuery(id+"F8.wireOp",EDGE,"E11.top"),sQuery(id+"F8.wireOp",EDGE,"E11.left"),sQuery(id+"F8.wireOp",EDGE,"E11.right")])],"isStart":true}),makeQuery(id+"F9.opExtrude","CAP_FACE",FACE,{"disambiguationData":[OSD([sQuery(id+"F8.wireOp",EDGE,"E12.bottom"),sQuery(id+"F8.wireOp",EDGE,"E12.top"),sQuery(id+"F8.wireOp",EDGE,"E12.left"),sQuery(id+"F8.wireOp",EDGE,"E12.right")])],"isStart":true})]}),makeQuery(id+"F16.opExtrude","CAP_FACE",FACE,{"disambiguationData":[OSD([sQuery(id+"F15.wireOp",EDGE,"E18.bottom"),sQuery(id+"F15.wireOp",EDGE,"E18.top"),sQuery(id+"F15.wireOp",EDGE,"E18.left"),sQuery(id+"F15.wireOp",EDGE,"E18.right")])],"isStart":true}),makeQuery(id+"F16.opExtrude","CAP_FACE",FACE,{"disambiguationData":[OSD([sQuery(id+"F15.wireOp",EDGE,"E19.bottom"),sQuery(id+"F15.wireOp",EDGE,"E19.top"),sQuery(id+"F15.wireOp",EDGE,"E19.left"),sQuery(id+"F15.wireOp",EDGE,"E19.right")])],"isStart":true})]}),makeQuery(id+"F34.opExtrude","CAP_FACE",FACE,{"disambiguationData":[OSD([sQuery(id+"F33.wireOp",EDGE,"E27.bottom"),sQuery(id+"F33.wireOp",EDGE,"E27.top"),sQuery(id+"F33.wireOp",EDGE,"E27.left"),sQuery(id+"F33.wireOp",EDGE,"E27.right")])],"isStart":true})]});
            fillet(context, id + "F35", {"entities" : qUnion([Q0]), "radius" : .5 * mm, "tangentPropagation" : true, "allowEdgeOverflow" : false});
        }
    });
